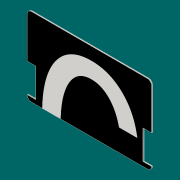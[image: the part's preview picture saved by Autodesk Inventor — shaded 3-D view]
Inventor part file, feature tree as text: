
AUTODESK INVENTOR PART (.ipt)
format: ipt  version: 2016 (Build 200138000, 138)  size: 220,160 bytes
history: native  units: mm
features: sketch x5, extrude x3, projected_geometry x3, other x2, fillet x1, mirror x1
ambient origin geometry x8: Origin, YZ Plane, XZ Plane, XY Plane, X Axis, Y Axis, Z Axis, Center Point
bodies: Solid1 (feature_tree)
feature tree (15):
  extrude  "Extrusion1"  Depth=53.98mm
  fillet  "Fillet1"  Radius=0.76mm
  extrude  "Extrusion2"  Depth=2.88mm
  extrude  "Extrusion3"  Depth=5.588mm
  mirror  "Mirror1"
  other  "Decal1"
  other  "Decal2"
  sketch  "Sketch1"  dims[d0=85.6mm d1=53.98mm d2=0.76mm]
  sketch  "Sketch2"  dims[d3=0.0mm d4=2.88mm]
  projected_geometry  "Projected Loop1"
  sketch  "Sketch3"  dims[d5=5.588mm d6=5.588mm]
  sketch  "Sketch4"  dims[d7=3.0mm]
  projected_geometry  "Projected Loop2"
  sketch  "Sketch5"  dims[d8=3.0mm d9=20.0mm d10=20.0mm d11=0.76mm d12=0.0mm d13=3.0mm d14=3.0mm d15=0.76mm d16=1.5mm d17=1.5mm d18=1.5mm d19=0.76mm d20=0.0mm]
  projected_geometry  "Projected Loop3"
